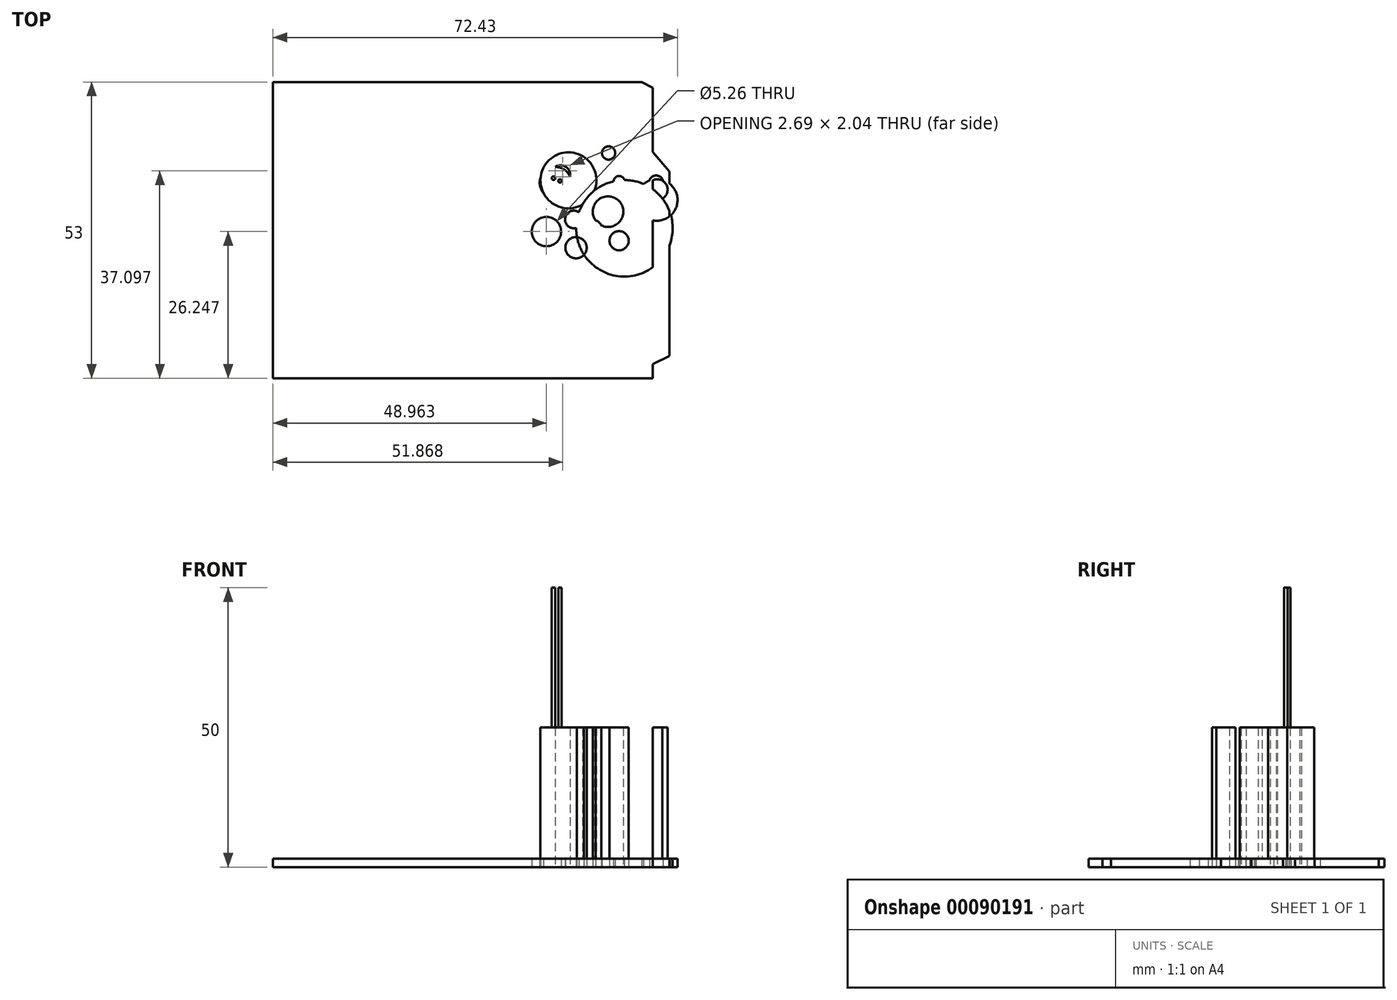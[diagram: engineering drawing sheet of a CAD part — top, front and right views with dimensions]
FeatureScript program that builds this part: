
annotation { "Feature Type Name" : "Feature", "Feature Type Description" : "" }
export const myFeature = defineFeature(function(context is Context, id is Id, definition is map)
    precondition{}
    {
        {
            var Q0;
            Q0=qCreatedBy(makeId("Top.planeOp"),FACE);
            var sketch = newSketch(context, id + "F0", { "sketchPlane" : qUnion([Q0])});
            skLineSegment(sketch, "E0.bottom", {"start": v(0, 0) * mm, "end": v(68, 0) * mm});
            skLineSegment(sketch, "E0.top", {"start": v(0, 53) * mm, "end": v(66, 53) * mm});
            skLineSegment(sketch, "E0.left", {"start": v(0, 0) * mm, "end": v(0, 53) * mm});
            skLineSegment(sketch, "E0.right", {"start": v(68, 0) * mm, "end": v(68, 52) * mm});
            skPoint(sketch, "E1", {"position": v(68, 37) * mm});
            skPoint(sketch, "E2", {"position": v(68, 40.5) * mm});
            skLineSegment(sketch, "E3", {"start": v(68, 37) * mm, "end": v(71, 37) * mm});
            skLineSegment(sketch, "E4", {"start": v(68, 40.5) * mm, "end": v(71, 37) * mm});
            skLineSegment(sketch, "E5", {"start": v(71, 37) * mm, "end": v(71, 4) * mm});
            skPoint(sketch, "E6", {"position": v(68, 2.5) * mm});
            skLineSegment(sketch, "E7", {"start": v(68, 2.5) * mm, "end": v(71, 4) * mm});
            skLineSegment(sketch, "E8", {"start": v(66, 53) * mm, "end": v(68, 52) * mm});
            skPoint(sketch, "E9.orphan", {"position": v(68, 53) * mm});
            skCircle(sketch, "E10", {"center": v(51.52, 36.4) * mm, "radius": 1.7 * mm});
            skCircle(sketch, "E11", {"center": v(52.9, 35.42) * mm, "radius": 5.01 * mm});
            skCircle(sketch, "E12", {"center": v(53.88, 28.41) * mm, "radius": 1.58 * mm});
            skCircle(sketch, "E13", {"center": v(48.96, 26.25) * mm, "radius": 2.63 * mm});
            skCircle(sketch, "E14", {"center": v(54.26, 23.36) * mm, "radius": 1.9 * mm});
            skCircle(sketch, "E15", {"center": v(57.4, 26.78) * mm, "radius": 1.51 * mm});
            skCircle(sketch, "E16", {"center": v(60, 29.81) * mm, "radius": 2.74 * mm});
            skCircle(sketch, "E17", {"center": v(61.97, 35.2) * mm, "radius": 1 * mm});
            skCircle(sketch, "E18", {"center": v(60.09, 40.31) * mm, "radius": 1.2 * mm});
            skCircle(sketch, "E19", {"center": v(61.97, 24.6) * mm, "radius": 1.72 * mm});
            skCircle(sketch, "E20", {"center": v(59.85, 21.67) * mm, "radius": 1.51 * mm});
            skCircle(sketch, "E21", {"center": v(68.61, 35.01) * mm, "radius": 1.27 * mm});
            skCircle(sketch, "E22", {"center": v(68.8, 33.75) * mm, "radius": 1.86 * mm});
            skCircle(sketch, "E23", {"center": v(68.71, 31.9) * mm, "radius": 3.72 * mm});
            skCircle(sketch, "E24", {"center": v(62.93, 26.83) * mm, "radius": 8.64 * mm});
            skCircle(sketch, "E25", {"center": v(50.59, 34.97) * mm, "radius": 2.83 * mm});
            skSolve(sketch);
        }
        {
            var Q0;
            Q0=qSketchRegion(id+"F0",true);
            extrude(context, id + "F1", {"entities" : qUnion([Q0]), "depth" : 1.5 * mm});
        }
        {
            var Q0;
            {var subQ0=sQuery(id+"F0.wireOp",EDGE,"E25");var subQ1=sQuery(id+"F0.wireOp",EDGE,"E10");var subQ2=makeQuery(id+"F0.imprint","INTERSECT",VERTEX,{"disambiguationData":[OD(0.0)],"derivedFrom":[subQ1,subQ0]});Q0=makeQuery(id+"F0.imprint","IMPRINT",FACE,{"disambiguationData":[TD([[makeQuery(id+"F0.imprint","IMPRINT",EDGE,{"disambiguationData":[TD([[subQ2,-1.0]])],"derivedFrom":subQ1}),-1.0]])]});}
            var Q1;
            {var subQ0=sQuery(id+"F0.wireOp",EDGE,"E25");var subQ1=sQuery(id+"F0.wireOp",EDGE,"E10");var subQ2=makeQuery(id+"F0.imprint","INTERSECT",VERTEX,{"disambiguationData":[OD(0.0)],"derivedFrom":[subQ1,subQ0]});Q1=makeQuery(id+"F0.imprint","IMPRINT",FACE,{"disambiguationData":[TD([[makeQuery(id+"F0.imprint","IMPRINT",EDGE,{"disambiguationData":[TD([[subQ2,-1.0]])],"derivedFrom":subQ1}),1.0]])]});}
            var Q2;
            {var subQ4=sQuery(id+"F0.wireOp",EDGE,"E25");var subQ6=sQuery(id+"F0.wireOp",EDGE,"E10");var subQ9=makeQuery(id+"F0.imprint","INTERSECT",VERTEX,{"disambiguationData":[OD(0.0)],"derivedFrom":[subQ6,subQ4]});Q2=makeQuery(id+"F0.imprint","IMPRINT",FACE,{"disambiguationData":[TD([[makeQuery(id+"F0.imprint","IMPRINT",EDGE,{"disambiguationData":[TD([[subQ9,1.0]])],"derivedFrom":subQ6}),-1.0]])]});}
            var Q3;
            {var subQ0=sQuery(id+"F0.wireOp",EDGE,"E16");var subQ1=sQuery(id+"F0.wireOp",EDGE,"E15");var subQ2=makeQuery(id+"F0.imprint","INTERSECT",VERTEX,{"disambiguationData":[OD(0.0)],"derivedFrom":[subQ1,subQ0]});Q3=makeQuery(id+"F0.imprint","IMPRINT",FACE,{"disambiguationData":[TD([[makeQuery(id+"F0.imprint","IMPRINT",EDGE,{"disambiguationData":[TD([[subQ2,1.0]])],"derivedFrom":subQ1}),-1.0]])]});}
            var Q4;
            {var subQ0=sQuery(id+"F0.wireOp",EDGE,"E24");var subQ1=sQuery(id+"F0.wireOp",EDGE,"E0.right");var subQ2=makeQuery(id+"F0.imprint","INTERSECT",VERTEX,{"disambiguationData":[OD(1.0)],"derivedFrom":[subQ1,subQ0]});Q4=makeQuery(id+"F0.imprint","IMPRINT",FACE,{"disambiguationData":[TD([[makeQuery(id+"F0.imprint","IMPRINT",EDGE,{"disambiguationData":[TD([[subQ2,-1.0]])],"derivedFrom":subQ1}),-1.0]])]});}
            var Q5;
            {var subQ0=sQuery(id+"F0.wireOp",EDGE,"E21");var subQ1=sQuery(id+"F0.wireOp",EDGE,"E0.right");var subQ2=makeQuery(id+"F0.imprint","INTERSECT",VERTEX,{"disambiguationData":[OD(0.0)],"derivedFrom":[subQ1,subQ0]});Q5=makeQuery(id+"F0.imprint","IMPRINT",FACE,{"disambiguationData":[TD([[makeQuery(id+"F0.imprint","IMPRINT",EDGE,{"disambiguationData":[TD([[subQ2,-1.0]])],"derivedFrom":subQ1}),-1.0]])]});}
            var Q6;
            Q6=makeQuery(id+"F0.imprint","IMPRINT",FACE,{"disambiguationData":[TD([[makeQuery(id+"F0.imprint","IMPRINT",EDGE,{"derivedFrom":sQuery(id+"F0.wireOp",EDGE,"E19")}),1.0]])]});
            var Q7;
            {var subQ0=sQuery(id+"F0.wireOp",EDGE,"E24");var subQ1=sQuery(id+"F0.wireOp",EDGE,"E14");var subQ2=makeQuery(id+"F0.imprint","INTERSECT",VERTEX,{"disambiguationData":[OD(0.0)],"derivedFrom":[subQ1,subQ0]});Q7=makeQuery(id+"F0.imprint","IMPRINT",FACE,{"disambiguationData":[TD([[makeQuery(id+"F0.imprint","IMPRINT",EDGE,{"disambiguationData":[TD([[subQ2,1.0]])],"derivedFrom":subQ1}),1.0]])]});}
            extrude(context, id + "F2", {"entities" : qUnion([Q0, Q1, Q2, Q3, Q4, Q5, Q6, Q7]), "operationType" : NewBodyOperationType.ADD, "depth" : 25 * mm});
        }
        {
            var Q0;
            Q0=makeQuery(id+"F2.opExtrude","CAP_FACE",FACE,{"disambiguationData":[OSD([sQuery(id+"F0.wireOp",EDGE,"E10"),sQuery(id+"F0.wireOp",EDGE,"E11"),sQuery(id+"F0.wireOp",EDGE,"E24"),sQuery(id+"F0.wireOp",EDGE,"E25")])],"isStart":false});
            var sketch = newSketch(context, id + "F3", { "sketchPlane" : qUnion([Q0])});
            skCircle(sketch, "E26", {"center": v(51.38, 35.32) * mm, "radius": 0.3 * mm});
            skCircle(sketch, "E27", {"center": v(50.24, 35.81) * mm, "radius": 0.32 * mm});
            skSolve(sketch);
        }
        {
            var Q0;
            Q0=makeQuery(id+"F3.imprint","IMPRINT",FACE,{"disambiguationData":[TD([[makeQuery(id+"F3.imprint","IMPRINT",EDGE,{"derivedFrom":sQuery(id+"F3.wireOp",EDGE,"E26")}),1.0]])]});
            var Q1;
            Q1=makeQuery(id+"F3.imprint","IMPRINT",FACE,{"disambiguationData":[TD([[makeQuery(id+"F3.imprint","IMPRINT",EDGE,{"derivedFrom":sQuery(id+"F3.wireOp",EDGE,"E27")}),1.0]])]});
            extrude(context, id + "F4", {"entities" : qUnion([Q0, Q1]), "operationType" : NewBodyOperationType.ADD, "oppositeDirection" : true, "depth" : 25 * mm});
        }
        {
            var Q0;
            Q0 = qSketchRegion(id + "F3", true);
            extrude(context, id + "F5", {"entities" : qUnion([Q0]), "operationType" : NewBodyOperationType.ADD, "depth" : 25 * mm});
        }
    });
